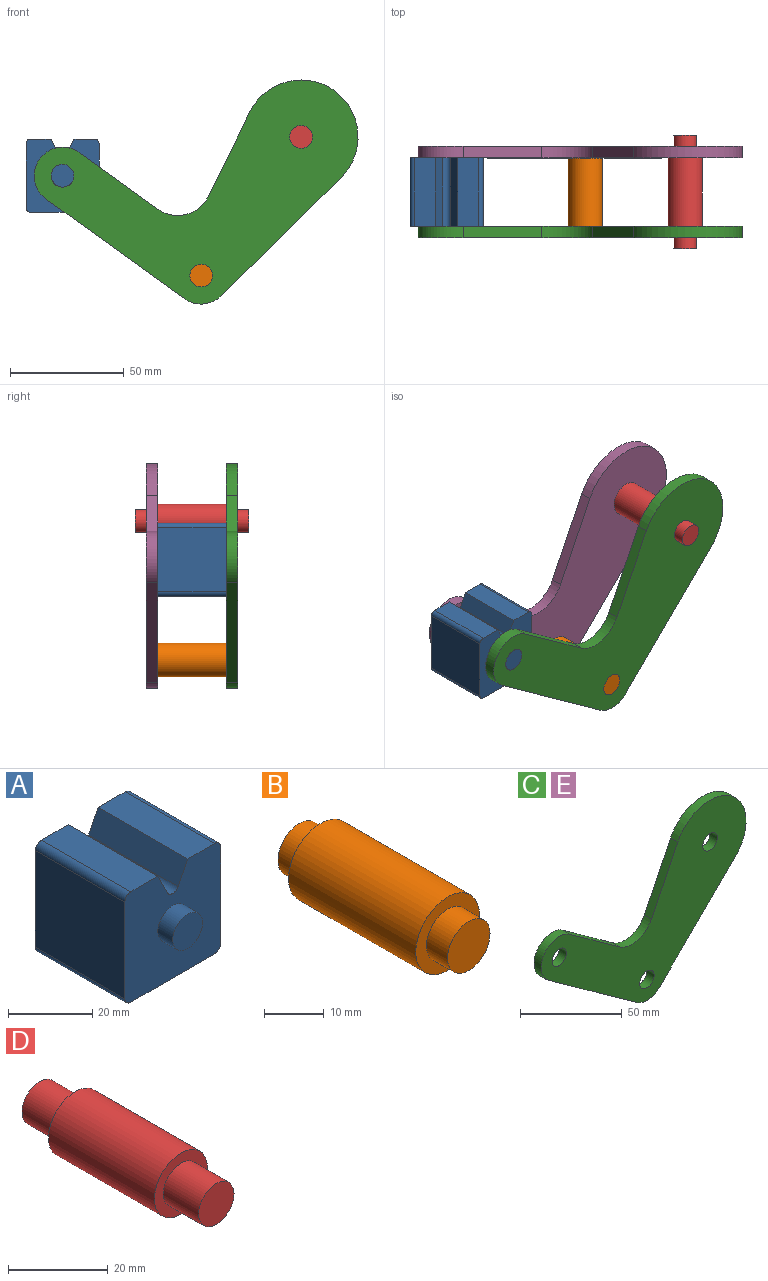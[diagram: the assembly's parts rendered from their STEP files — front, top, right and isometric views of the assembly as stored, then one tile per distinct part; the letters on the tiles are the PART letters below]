
ASSEMBLY  parts=5 mates=2
PART A: 18 faces, bbox 32.1x40x32.1 mm
  f0: plane 30x6.42mm, normal (0.89,0,0.45), area 215.4mm2, adj f4,f6,f10,f13
  f1: plane 30x6.42mm, normal (-0.89,0,0.45), area 215.4mm2, adj f2,f4,f10,f13
  f2: plane 30x9.04mm, normal (0,0,1), area 271.2mm2, adj f1,f4,f10,f14
  f3: plane 30x28.08mm, normal (1,0,0), area 842.3mm2, adj f4,f10,f14,f15
  f4: plane 32.08x32.08mm, normal (0,-1,0), area 900.6mm2, adj f0,f1,f2,f3,f5,f6,f7,f9
  f5: plane 30x28.08mm, normal (0,0,-1), area 842.3mm2, adj f4,f10,f15,f16
  f6: plane 30x9.04mm, normal (0,0,1), area 271.2mm2, adj f0,f4,f10,f17
  f7: plane 30x28.08mm, normal (-1,0,0), area 842.3mm2, adj f4,f10,f16,f17
  f8: plane 10x10mm, normal (0,-1,0), area 78.5mm2, adj f9
  f9: cylinder r=5mm len=10mm, axis (0,1,0), area 157.1mm2, adj f4,f8
  f10: plane 32.08x32.08mm, normal (0,1,0), area 900.6mm2, adj f0,f1,f2,f3,f5,f6,f7,f12
  f11: plane 10x10mm, normal (0,1,0), area 78.5mm2, adj f12
  f12: cylinder r=5mm len=10mm, axis (0,-1,0), area 157.1mm2, adj f10,f11
  f13: cylinder r=2mm len=30mm, axis (0,1,0), area 132.9mm2, adj f0,f1,f4,f10
  f14: cylinder r=2mm len=30mm, axis (0,1,0), area 94.2mm2, adj f2,f3,f4,f10
  f15: cylinder r=2mm len=30mm, axis (0,-1,0), area 94.2mm2, adj f3,f4,f5,f10
  f16: cylinder r=2mm len=30mm, axis (0,1,0), area 94.2mm2, adj f4,f5,f7,f10
  f17: cylinder r=2mm len=30mm, axis (0,-1,0), area 94.2mm2, adj f4,f6,f7,f10
PART B: 7 faces, bbox 15x40x15 mm
  f0: cylinder r=7.5mm len=30mm, axis (0,-1,0), area 1413.7mm2, adj f2,f5
  f1: cylinder r=5mm len=10mm, axis (0,-1,0), area 157.1mm2, adj f2,f3
  f2: plane 15x15mm, normal (0,-1,0), area 98.2mm2, adj f0,f1
  f3: plane 10x10mm, normal (0,-1,0), area 78.5mm2, adj f1
  f4: cylinder r=5mm len=10mm, axis (0,1,0), area 157.1mm2, adj f5,f6
  f5: plane 15x15mm, normal (0,1,0), area 98.2mm2, adj f0,f4
  f6: plane 10x10mm, normal (0,1,0), area 78.5mm2, adj f4
PART C: 13 faces, bbox 142.2x5x98.4 mm
  f0: plane 52.61x51.97mm, normal (0.7,0,-0.71), area 369.8mm2, adj f1,f9,f11,f12
  f1: cylinder r=25mm len=47.44mm, axis (0,-1,0), area 434.6mm2, adj f0,f2,f11,f12
  f2: plane 37.17x18.26mm, normal (-0.9,0,0.44), area 207.1mm2, adj f1,f3,f11,f12
  f3: cylinder r=15mm len=22.23mm, axis (0,-1,0), area 130.4mm2, adj f2,f4,f11,f12
  f4: plane 34.46x24.81mm, normal (0.58,0,0.81), area 212.3mm2, adj f3,f5,f11,f12
  f5: cylinder r=12.5mm len=22.64mm, axis (0,-1,0), area 196.3mm2, adj f4,f6,f11,f12
  f6: plane 60.86x43.82mm, normal (-0.58,0,-0.81), area 375mm2, adj f5,f9,f11,f12
  f7: cylinder r=5mm len=10mm, axis (0,-1,0), area 157.1mm2, adj f11,f12
  f8: cylinder r=5mm len=10mm, axis (0,-1,0), area 157.1mm2, adj f11,f12
  f9: cylinder r=12.5mm len=16.09mm, axis (0,-1,0), area 87.7mm2, adj f0,f6,f11,f12
  f10: cylinder r=5mm len=10mm, axis (0,-1,0), area 157.1mm2, adj f11,f12
  f11: plane 142.19x98.36mm, normal (0,1,0), area 5739.8mm2, adj f0,f1,f2,f3,f4,f5,f6,f7
  f12: plane 142.19x98.36mm, normal (0,-1,0), area 5739.8mm2, adj f0,f1,f2,f3,f4,f5,f6,f7
PART D: 7 faces, bbox 15x50x15 mm
  f0: cylinder r=7.5mm len=30mm, axis (0,-1,0), area 1413.7mm2, adj f2,f5
  f1: cylinder r=5mm len=10mm, axis (0,1,0), area 314.2mm2, adj f2,f3
  f2: plane 15x15mm, normal (0,-1,0), area 98.2mm2, adj f0,f1
  f3: plane 10x10mm, normal (0,-1,0), area 78.5mm2, adj f1
  f4: cylinder r=5mm len=10mm, axis (0,-1,0), area 314.2mm2, adj f5,f6
  f5: plane 15x15mm, normal (0,1,0), area 98.2mm2, adj f0,f4
  f6: plane 10x10mm, normal (0,1,0), area 78.5mm2, adj f4
PART E: same geometry as C
PLACE A t=(18.9,-11.44,69.63)mm
PLACE B t=(18.9,-11.44,69.63)mm
PLACE C t=(18.9,-11.44,69.63)mm
PLACE D t=(18.9,-11.44,69.63)mm
PLACE E t=(18.9,23.56,69.63)mm
MATE fastened B.f0 <-> E.f7  axis (0,1,0) through (-24.92,28.56,8.77)mm
MATE revolute A.f9 <-> C.f5  axis (0,-1,0) through (-85.79,-11.44,52.59)mm
